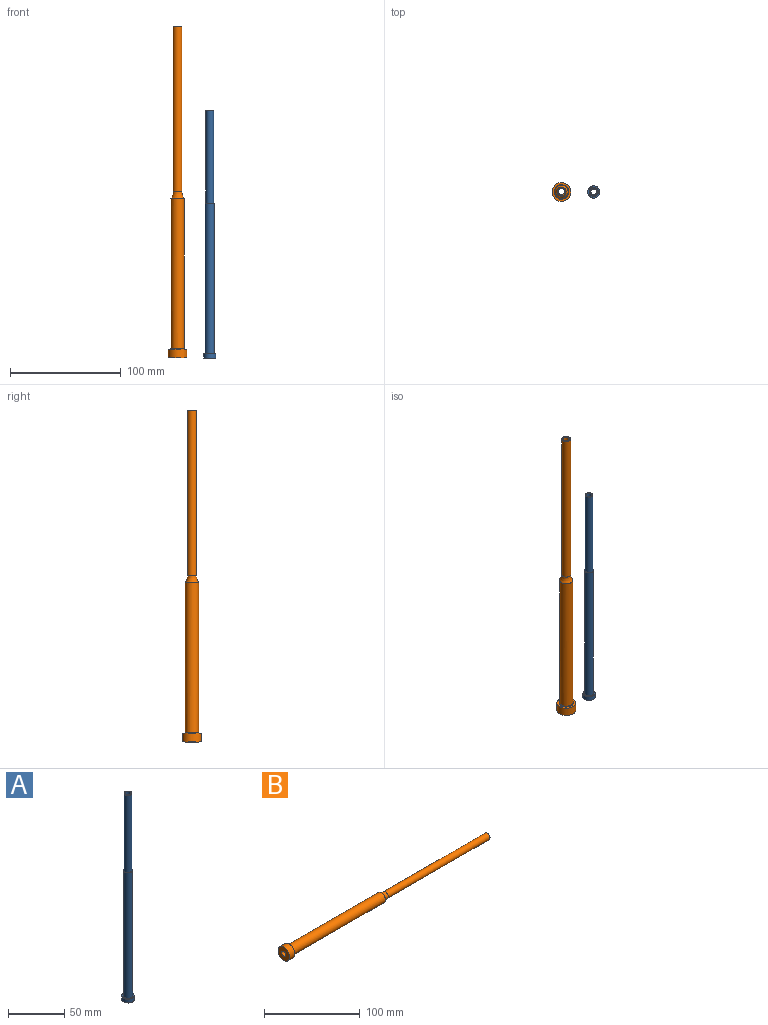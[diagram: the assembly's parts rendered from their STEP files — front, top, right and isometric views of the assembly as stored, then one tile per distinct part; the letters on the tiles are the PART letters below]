
ASSEMBLY  parts=2 mates=1
PART A: 8 faces, bbox 11x11.2x223.6 mm
  f0: plane 11.2x11.01mm, normal (0,0,-1), area 73mm2, adj f1,f2
  f1: cylinder r=5.5mm len=11mm, axis (0,0,1), area 138.2mm2, adj f0,f3
  f2: cylinder r=2.65mm len=223.57mm, axis (0,0,-1), area 3722.6mm2, adj f0,f4
  f3: plane 11.2x11.01mm, normal (0,0,1), area 44.8mm2, adj f1,f5
  f4: plane 7.09x7mm, normal (0,0,1), area 16.4mm2, adj f2,f6
  f5: cylinder r=4mm len=136mm, axis (0,0,-1), area 3418.1mm2, adj f3,f7
  f6: cylinder r=3.5mm len=83.57mm, axis (0,0,-1), area 1837.8mm2, adj f4,f7
  f7: plane 8.15x8.01mm, normal (0,0,1), area 11.8mm2, adj f5,f6
PART B: 11 faces, bbox 300x17x17 mm
  f0: cylinder r=2.75mm len=100mm, axis (1,0,0), area 1727.9mm2, adj f1,f7
  f1: cone r=2.88mm half-angle=26.6deg, axis (-1,0,0), area 10.1mm2, adj f0,f2
  f2: cylinder r=3mm len=199.5mm, axis (1,0,0), area 3760.5mm2, adj f1,f10
  f3: torus R=6.5mm, axis (-1,0,0), area 30.5mm2, adj f4,f5
  f4: cylinder r=6mm len=135.5mm, axis (1,0,0), area 5108.2mm2, adj f3,f8
  f5: plane 17x17mm, normal (1,0,0), area 94.2mm2, adj f3,f9
  f6: cylinder r=4mm len=150mm, axis (1,0,0), area 3769.9mm2, adj f7,f8
  f7: plane 8x8mm, normal (1,0,0), area 26.5mm2, adj f0,f6
  f8: torus R=14mm, axis (1,0,0), area 189.1mm2, adj f4,f6
  f9: cylinder r=8.5mm len=17mm, axis (1,0,0), area 427.3mm2, adj f5,f10
  f10: plane 17x17mm, normal (-1,0,0), area 198.7mm2, adj f2,f9
PLACE A t=(26.5,0,0)mm
PLACE B rot(axis=(0,-1,0),90deg) t=(-188.48,-147.92,-200)mm
MATE planar B.f0 <-> A.f0  axis (0,0,-1) through (-188.48,-147.92,-200)mm
